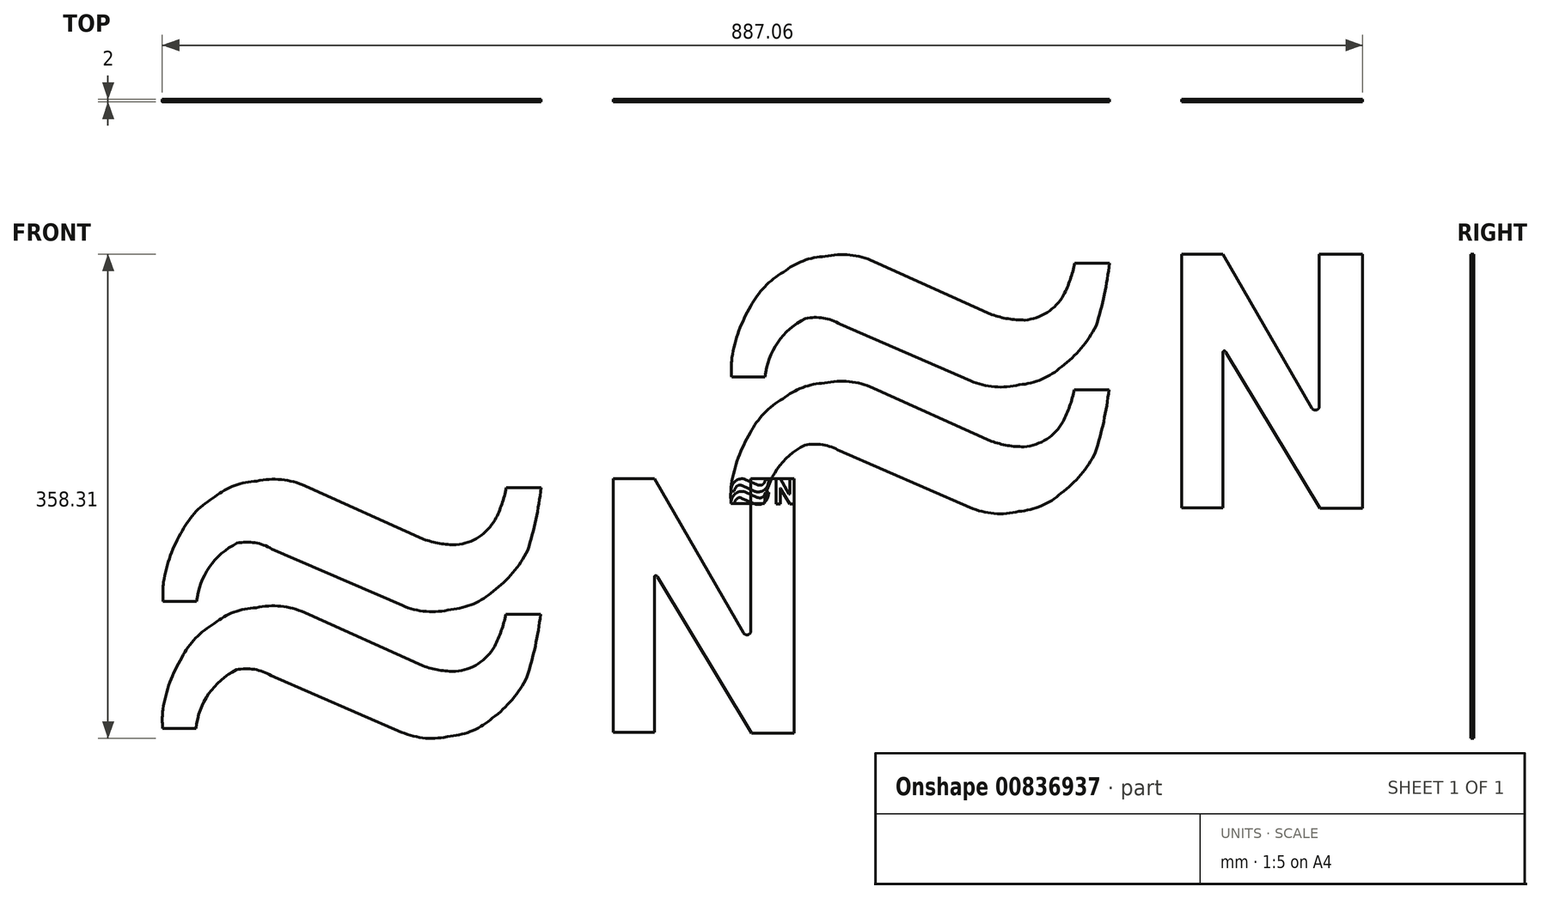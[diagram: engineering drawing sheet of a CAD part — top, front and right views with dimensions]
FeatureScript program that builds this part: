
annotation { "Feature Type Name" : "Feature", "Feature Type Description" : "" }
export const myFeature = defineFeature(function(context is Context, id is Id, definition is map)
    precondition{}
    {
        {
            var Q0;
            Q0=qCreatedBy(makeId("Front.planeOp"),FACE);
            var sketch = newSketch(context, id + "F0", { "sketchPlane" : qUnion([Q0])});
            skLineSegment(sketch, "E0", {"start": v(-24.05, 16.58) * mm, "end": v(-21, 16.58) * mm});
            skLineSegment(sketch, "E1", {"start": v(-21, 16.58) * mm, "end": v(-21, 28.07) * mm});
            skLineSegment(sketch, "E2", {"start": v(-10.67, 16.52) * mm, "end": v(-10.67, 35.34) * mm});
            skLineSegment(sketch, "E3", {"start": v(-10.67, 35.34) * mm, "end": v(-13.87, 35.34) * mm});
            skLineSegment(sketch, "E4", {"start": v(-13.87, 35.34) * mm, "end": v(-13.87, 24.08) * mm});
            skLineSegment(sketch, "E5", {"start": v(-14.42, 23.93) * mm, "end": v(-21, 35.34) * mm});
            skLineSegment(sketch, "E6", {"start": v(-21, 35.34) * mm, "end": v(-24.05, 35.34) * mm});
            skLineSegment(sketch, "E7", {"start": v(-24.05, 35.34) * mm, "end": v(-24.05, 16.58) * mm});
            skLineSegment(sketch, "E8", {"start": v(-57.3, 26.25) * mm, "end": v(-54.83, 26.25) * mm});
            skArc(sketch, "E9", {"start": v(-51.85, 30.57) * mm, "mid": v(-53.9, 28.8) * mm, "end": v(-54.83, 26.25) * mm});
            skArc(sketch, "E10", {"start": v(-49.28, 30.14) * mm, "mid": v(-50.52, 30.6) * mm, "end": v(-51.85, 30.57) * mm});
            skLineSegment(sketch, "E11", {"start": v(-49.28, 30.14) * mm, "end": v(-39.64, 25.96) * mm});
            skArc(sketch, "E12", {"start": v(-39.64, 25.96) * mm, "mid": v(-37.86, 25.52) * mm, "end": v(-36.04, 25.67) * mm});
            skArc(sketch, "E13", {"start": v(-36.04, 25.67) * mm, "mid": v(-34.36, 26.08) * mm, "end": v(-32.91, 27.02) * mm});
            skArc(sketch, "E14", {"start": v(-32.91, 27.02) * mm, "mid": v(-31.46, 28.37) * mm, "end": v(-30.37, 30.03) * mm});
            skArc(sketch, "E15", {"start": v(-30.37, 30.03) * mm, "mid": v(-29.76, 32.33) * mm, "end": v(-29.37, 34.67) * mm});
            skLineSegment(sketch, "E16", {"start": v(-29.37, 34.67) * mm, "end": v(-31.94, 34.67) * mm});
            skArc(sketch, "E17", {"start": v(-32.76, 32.3) * mm, "mid": v(-32.27, 33.46) * mm, "end": v(-31.94, 34.67) * mm});
            skArc(sketch, "E18", {"start": v(-35.64, 30.45) * mm, "mid": v(-33.98, 31.02) * mm, "end": v(-32.76, 32.3) * mm});
            skArc(sketch, "E19", {"start": v(-38.06, 30.87) * mm, "mid": v(-36.87, 30.55) * mm, "end": v(-35.64, 30.45) * mm});
            skLineSegment(sketch, "E20", {"start": v(-38.06, 30.87) * mm, "end": v(-46.8, 34.8) * mm});
            skArc(sketch, "E21", {"start": v(-46.8, 34.8) * mm, "mid": v(-48.56, 35.27) * mm, "end": v(-50.38, 35.16) * mm});
            skArc(sketch, "E22", {"start": v(-50.38, 35.16) * mm, "mid": v(-52.02, 34.83) * mm, "end": v(-53.46, 34) * mm});
            skArc(sketch, "E23", {"start": v(-55.88, 31.48) * mm, "mid": v(-56.76, 29.65) * mm, "end": v(-57.27, 27.68) * mm});
            skArc(sketch, "E24", {"start": v(-53.46, 34) * mm, "mid": v(-54.85, 32.92) * mm, "end": v(-55.88, 31.48) * mm});
            skArc(sketch, "E25", {"start": v(-57.27, 27.68) * mm, "mid": v(-57.32, 26.96) * mm, "end": v(-57.3, 26.25) * mm});
            skLineSegment(sketch, "E26", {"start": v(-13.81, 16.52) * mm, "end": v(-10.67, 16.52) * mm});
            skPoint(sketch, "E27.start.orphan", {"position": v(-13.87, 16.14) * mm});
            skLineSegment(sketch, "E28", {"start": v(-20.78, 28.07) * mm, "end": v(-13.81, 16.52) * mm});
            skArc(sketch, "E29", {"start": v(-20.78, 28.07) * mm, "mid": v(-20.89, 28.17) * mm, "end": v(-21, 28.07) * mm});
            skPoint(sketch, "E30.visualSharp", {"position": v(-13.87, 22.98) * mm});
            skArc(sketch, "E30.filletArc", {"start": v(-14.42, 23.93) * mm, "mid": v(-14.08, 23.8) * mm, "end": v(-13.87, 24.08) * mm});
            skLineSegment(sketch, "E31", {"start": v(-57.34, 16.88) * mm, "end": v(-54.87, 16.88) * mm});
            skArc(sketch, "E32", {"start": v(-51.89, 21.2) * mm, "mid": v(-53.93, 19.42) * mm, "end": v(-54.87, 16.88) * mm});
            skArc(sketch, "E33", {"start": v(-49.32, 20.77) * mm, "mid": v(-50.56, 21.23) * mm, "end": v(-51.89, 21.2) * mm});
            skLineSegment(sketch, "E34", {"start": v(-49.32, 20.77) * mm, "end": v(-39.68, 16.6) * mm});
            skArc(sketch, "E35", {"start": v(-39.68, 16.6) * mm, "mid": v(-37.9, 16.15) * mm, "end": v(-36.08, 16.3) * mm});
            skArc(sketch, "E36", {"start": v(-36.08, 16.3) * mm, "mid": v(-34.4, 16.71) * mm, "end": v(-32.95, 17.64) * mm});
            skArc(sketch, "E37", {"start": v(-32.95, 17.64) * mm, "mid": v(-31.5, 19) * mm, "end": v(-30.4, 20.66) * mm});
            skArc(sketch, "E38", {"start": v(-30.4, 20.66) * mm, "mid": v(-29.8, 22.96) * mm, "end": v(-29.41, 25.3) * mm});
            skLineSegment(sketch, "E39", {"start": v(-29.41, 25.3) * mm, "end": v(-31.98, 25.3) * mm});
            skArc(sketch, "E40", {"start": v(-32.8, 22.93) * mm, "mid": v(-32.31, 24.09) * mm, "end": v(-31.98, 25.3) * mm});
            skArc(sketch, "E41", {"start": v(-35.69, 21.08) * mm, "mid": v(-34.02, 21.65) * mm, "end": v(-32.8, 22.93) * mm});
            skArc(sketch, "E42", {"start": v(-38.1, 21.5) * mm, "mid": v(-36.91, 21.18) * mm, "end": v(-35.69, 21.08) * mm});
            skLineSegment(sketch, "E43", {"start": v(-38.1, 21.5) * mm, "end": v(-46.85, 25.43) * mm});
            skArc(sketch, "E44", {"start": v(-46.85, 25.43) * mm, "mid": v(-48.6, 25.9) * mm, "end": v(-50.42, 25.79) * mm});
            skArc(sketch, "E45", {"start": v(-50.42, 25.79) * mm, "mid": v(-52.06, 25.46) * mm, "end": v(-53.5, 24.63) * mm});
            skArc(sketch, "E46", {"start": v(-55.92, 22.11) * mm, "mid": v(-56.8, 20.28) * mm, "end": v(-57.31, 18.3) * mm});
            skArc(sketch, "E47", {"start": v(-53.5, 24.63) * mm, "mid": v(-54.9, 23.54) * mm, "end": v(-55.92, 22.11) * mm});
            skArc(sketch, "E48", {"start": v(-57.31, 18.3) * mm, "mid": v(-57.36, 17.6) * mm, "end": v(-57.34, 16.88) * mm});
            skSolve(sketch);
        }
        {
            var Q0;
            Q0 = qSketchRegion(id + "F0", true);
            extrude(context, id + "F1", {"entities" : qUnion([Q0]), "depth" : 0.2 * mm, "offsetDistance" : 25 * mm});
        }
        {
            var Q0;
            Q0=makeQuery(id+"F1.opExtrude","SWEPT_BODY",BODY,{"disambiguationData":[OSD([sQuery(id+"F0.wireOp",EDGE,"E8"),sQuery(id+"F0.wireOp",EDGE,"E9"),sQuery(id+"F0.wireOp",EDGE,"E10"),sQuery(id+"F0.wireOp",EDGE,"E11"),sQuery(id+"F0.wireOp",EDGE,"E12"),sQuery(id+"F0.wireOp",EDGE,"E13"),sQuery(id+"F0.wireOp",EDGE,"E14"),sQuery(id+"F0.wireOp",EDGE,"E15"),sQuery(id+"F0.wireOp",EDGE,"E16"),sQuery(id+"F0.wireOp",EDGE,"E17"),sQuery(id+"F0.wireOp",EDGE,"E18"),sQuery(id+"F0.wireOp",EDGE,"E19"),sQuery(id+"F0.wireOp",EDGE,"E20"),sQuery(id+"F0.wireOp",EDGE,"E21"),sQuery(id+"F0.wireOp",EDGE,"E22"),sQuery(id+"F0.wireOp",EDGE,"E23"),sQuery(id+"F0.wireOp",EDGE,"E24"),sQuery(id+"F0.wireOp",EDGE,"E25")])]});
            var Q1;
            Q1=makeQuery(id+"F1.opExtrude","SWEPT_BODY",BODY,{"disambiguationData":[OSD([sQuery(id+"F0.wireOp",EDGE,"E31"),sQuery(id+"F0.wireOp",EDGE,"E32"),sQuery(id+"F0.wireOp",EDGE,"E33"),sQuery(id+"F0.wireOp",EDGE,"E34"),sQuery(id+"F0.wireOp",EDGE,"E35"),sQuery(id+"F0.wireOp",EDGE,"E36"),sQuery(id+"F0.wireOp",EDGE,"E37"),sQuery(id+"F0.wireOp",EDGE,"E38"),sQuery(id+"F0.wireOp",EDGE,"E39"),sQuery(id+"F0.wireOp",EDGE,"E40"),sQuery(id+"F0.wireOp",EDGE,"E41"),sQuery(id+"F0.wireOp",EDGE,"E42"),sQuery(id+"F0.wireOp",EDGE,"E43"),sQuery(id+"F0.wireOp",EDGE,"E44"),sQuery(id+"F0.wireOp",EDGE,"E45"),sQuery(id+"F0.wireOp",EDGE,"E46"),sQuery(id+"F0.wireOp",EDGE,"E47"),sQuery(id+"F0.wireOp",EDGE,"E48")])]});
            var Q2;
            Q2=makeQuery(id+"F1.opExtrude","SWEPT_BODY",BODY,{"disambiguationData":[OSD([sQuery(id+"F0.wireOp",EDGE,"E0"),sQuery(id+"F0.wireOp",EDGE,"E1"),sQuery(id+"F0.wireOp",EDGE,"E2"),sQuery(id+"F0.wireOp",EDGE,"E3"),sQuery(id+"F0.wireOp",EDGE,"E4"),sQuery(id+"F0.wireOp",EDGE,"E5"),sQuery(id+"F0.wireOp",EDGE,"E6"),sQuery(id+"F0.wireOp",EDGE,"E7"),sQuery(id+"F0.wireOp",EDGE,"E26"),sQuery(id+"F0.wireOp",EDGE,"E28"),sQuery(id+"F0.wireOp",EDGE,"E29"),sQuery(id+"F0.wireOp",EDGE,"E30.filletArc")])]});
            var Q3;
            Q3=makeQuery(id+"F1.opExtrude","CAP_VERTEX",VERTEX,{"disambiguationData":[OSD([sQuery(id+"F0.wireOp",EDGE,"E31"),sQuery(id+"F0.wireOp",EDGE,"E48")])],"isStart":false});
            transform(context, id + "F2", {"entities" : qUnion([Q0, Q1, Q2]), "transformType" : TransformType.SCALE_UNIFORMLY, "scale" : 10, "scalePoint" : qUnion([Q3]), "makeCopy" : true});
        }
        {
            var Q0;
            Q0=makeQuery(id+"F1.opExtrude","SWEPT_BODY",BODY,{"disambiguationData":[OSD([sQuery(id+"F0.wireOp",EDGE,"E0"),sQuery(id+"F0.wireOp",EDGE,"E1"),sQuery(id+"F0.wireOp",EDGE,"E2"),sQuery(id+"F0.wireOp",EDGE,"E3"),sQuery(id+"F0.wireOp",EDGE,"E4"),sQuery(id+"F0.wireOp",EDGE,"E5"),sQuery(id+"F0.wireOp",EDGE,"E6"),sQuery(id+"F0.wireOp",EDGE,"E7"),sQuery(id+"F0.wireOp",EDGE,"E26"),sQuery(id+"F0.wireOp",EDGE,"E28"),sQuery(id+"F0.wireOp",EDGE,"E29"),sQuery(id+"F0.wireOp",EDGE,"E30.filletArc")])]});
            var Q1;
            Q1=makeQuery(id+"F1.opExtrude","SWEPT_BODY",BODY,{"disambiguationData":[OSD([sQuery(id+"F0.wireOp",EDGE,"E8"),sQuery(id+"F0.wireOp",EDGE,"E9"),sQuery(id+"F0.wireOp",EDGE,"E10"),sQuery(id+"F0.wireOp",EDGE,"E11"),sQuery(id+"F0.wireOp",EDGE,"E12"),sQuery(id+"F0.wireOp",EDGE,"E13"),sQuery(id+"F0.wireOp",EDGE,"E14"),sQuery(id+"F0.wireOp",EDGE,"E15"),sQuery(id+"F0.wireOp",EDGE,"E16"),sQuery(id+"F0.wireOp",EDGE,"E17"),sQuery(id+"F0.wireOp",EDGE,"E18"),sQuery(id+"F0.wireOp",EDGE,"E19"),sQuery(id+"F0.wireOp",EDGE,"E20"),sQuery(id+"F0.wireOp",EDGE,"E21"),sQuery(id+"F0.wireOp",EDGE,"E22"),sQuery(id+"F0.wireOp",EDGE,"E23"),sQuery(id+"F0.wireOp",EDGE,"E24"),sQuery(id+"F0.wireOp",EDGE,"E25")])]});
            var Q2;
            Q2=makeQuery(id+"F1.opExtrude","SWEPT_BODY",BODY,{"disambiguationData":[OSD([sQuery(id+"F0.wireOp",EDGE,"E31"),sQuery(id+"F0.wireOp",EDGE,"E32"),sQuery(id+"F0.wireOp",EDGE,"E33"),sQuery(id+"F0.wireOp",EDGE,"E34"),sQuery(id+"F0.wireOp",EDGE,"E35"),sQuery(id+"F0.wireOp",EDGE,"E36"),sQuery(id+"F0.wireOp",EDGE,"E37"),sQuery(id+"F0.wireOp",EDGE,"E38"),sQuery(id+"F0.wireOp",EDGE,"E39"),sQuery(id+"F0.wireOp",EDGE,"E40"),sQuery(id+"F0.wireOp",EDGE,"E41"),sQuery(id+"F0.wireOp",EDGE,"E42"),sQuery(id+"F0.wireOp",EDGE,"E43"),sQuery(id+"F0.wireOp",EDGE,"E44"),sQuery(id+"F0.wireOp",EDGE,"E45"),sQuery(id+"F0.wireOp",EDGE,"E46"),sQuery(id+"F0.wireOp",EDGE,"E47"),sQuery(id+"F0.wireOp",EDGE,"E48")])]});
            var Q3;
            Q3=makeQuery(id+"F1.opExtrude","CAP_VERTEX",VERTEX,{"disambiguationData":[OSD([sQuery(id+"F0.wireOp",EDGE,"E2"),sQuery(id+"F0.wireOp",EDGE,"E3")])],"isStart":false});
            transform(context, id + "F3", {"entities" : qUnion([Q0, Q1, Q2]), "transformType" : TransformType.SCALE_UNIFORMLY, "scale" : 10, "scalePoint" : qUnion([Q3]), "makeCopy" : true});
        }
    });
